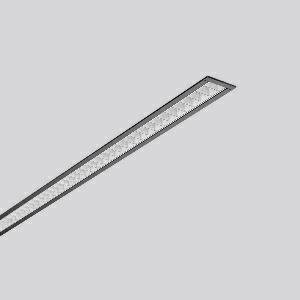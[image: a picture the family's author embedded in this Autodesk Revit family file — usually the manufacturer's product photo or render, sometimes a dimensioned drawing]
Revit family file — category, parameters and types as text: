
# Revit family: less_is_more_27_312177_003_ca46
name_source: partatom
category: Lighting Fixtures
units: mm (PartAtom-declared; Revit-internal decimal feet)

## family parameters
Cut with Voids When Loaded = No
Host = Face
Light Source = No
Part Type = Normal
Room Calculation Point = No
Round Connector Dimension = Use Diameter
Shared = No

## types (1)
- LESS IS MORE 27 (1 x LED Modul 830, 2350 lm, 3000)
    Apparent Load = 29 VA
    CIE Flux Codes = 90 99 100 100 100
    Color Rendering = 80
    Color Temperature = 3000
    Default Elevation = 1800 mm
    Description = Series: LESS IS MORE 27
Recessed ceiling and wall luminaire with slim design. Housing: extruded aluminium profile, powder-coated. End cap aluminium powder-coated. High polish aluminium micro grid. Perfect for office areas (RUG < 19) and environments with computer screens in accordance with EN 12464-1. Suitable for Recessed ceiling mounting, wall (recessed). External driver with connecting cable. 
Colour: deep black, matt (RAL 9005)
Length: 1014 mm
Width: 38 mm
Height: 2 mm
Cut-out length: 1006 mm
Cut-out width: 30 mm
Recess height: 45-60 mm
Luminaire: recess height: 37 mm
Lamp: LED
Socket: without socket
Colour temperature: 3000K
Colour rendering index (CRI): 82
System power: 29 W
Rated luminous flux: 2350 lm
Luminous efficiency: 81 lm/W
Control gear: Regulated power supply
Protection class: II
Type of protection: IP 20
    Height = 0 mm  [stored 0 ft]
    Lamp = 1 x LED Modul 830
    Lamp Light Flux = 2350 lm
    Lamp count = 1
    Length = 1014 mm
    Lifetime = 50000 h
    Luminous efficacy = 81 lm/W
    Manufacturer = RZB
    ModVariant = No
    Model = 312177.003
    Mounting Place = Ceiling, Wall
    Mounting Type = Recessed
    Number of Poles = 1
    OnlyDefault = Yes
    Power Factor = 1
    Product Name = LESS IS MORE 27
    Product group = Recessed LED linear luminaires
    ProductGroupID = 407
    Protection Class = Protection class II
    Protection Degree = IP 20
    RLX_Detail_Level = 1
    RLX_Emergency_Light_Flux = 0 lm
    RLX_Emergency_Type = 0
    RLX_Emergency_Type_DB = No
    RlxData = <blob elided: 29885 chars, md5=eb6ca94f>
    Socket = socket
    Standby Power = 0 W
    System Light Flux = 2350 lm
    System Power = 29 W
    Type Comments = Product without accessories
    Type Image = 312177.003.jpg
    URL = http://relux.com
    VarID = ---
    Voltage = 230 V
    Voltage Range = 220-240 V
    Weight = 0.00 kg
    Width = 38 mm

note: [stored X ft] marks values corroborated as IEEE doubles in the binary element streams (Revit-internal decimal feet)

## geometry (parser evidence)
native form markers: Blend x4, Sweep x9
no freeform markers — native parametric forms only
